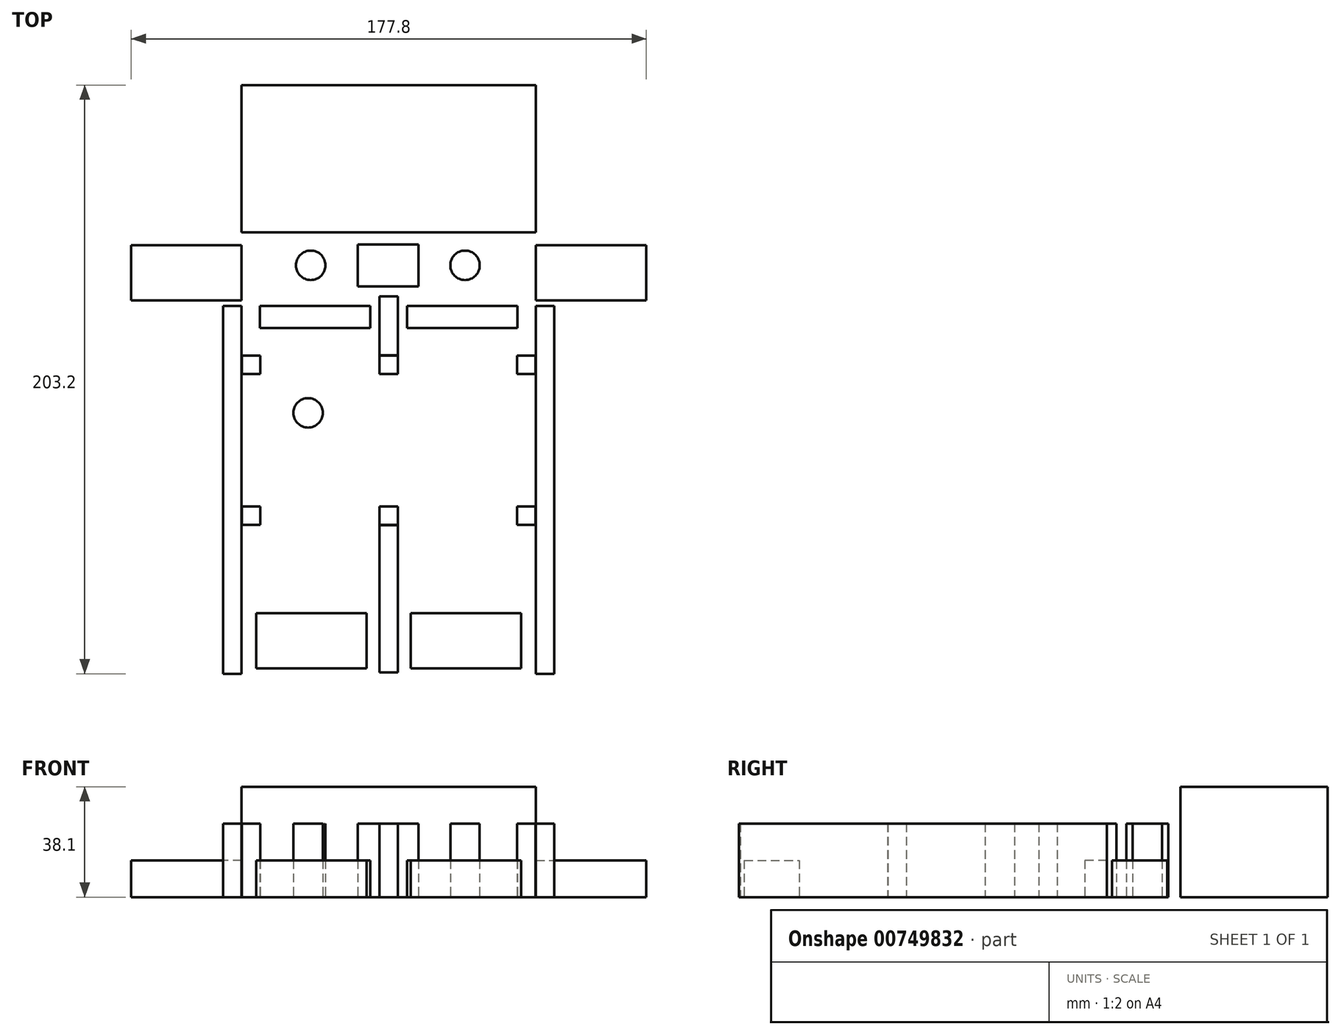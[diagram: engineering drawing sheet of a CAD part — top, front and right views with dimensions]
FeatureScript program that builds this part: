
annotation { "Feature Type Name" : "Feature", "Feature Type Description" : "" }
export const myFeature = defineFeature(function(context is Context, id is Id, definition is map)
    precondition{}
    {
        {
            var Q0;
            Q0=qCreatedBy(makeId("Top.planeOp"),FACE);
            var sketch = newSketch(context, id + "F0", { "sketchPlane" : qUnion([Q0])});
            skLineSegment(sketch, "E0.bottom", {"start": v(50.8, 25.4) * mm, "end": v(-50.8, 25.4) * mm});
            skLineSegment(sketch, "E0.top", {"start": v(50.8, -25.4) * mm, "end": v(-50.8, -25.4) * mm});
            skLineSegment(sketch, "E0.left", {"start": v(50.8, 25.4) * mm, "end": v(50.8, -25.4) * mm});
            skLineSegment(sketch, "E0.right", {"start": v(-50.8, 25.4) * mm, "end": v(-50.8, -25.4) * mm});
            skPoint(sketch, "E0.middle", {"position": v(0, 0) * mm});
            skSolve(sketch);
        }
        {
            var Q0;
            Q0=makeQuery(id+"F0.imprint","IMPRINT",FACE,{"disambiguationData":[TD([[makeQuery(id+"F0.imprint","IMPRINT",EDGE,{"derivedFrom":sQuery(id+"F0.wireOp",EDGE,"E0.bottom")}),1.0]])]});
            extrude(context, id + "F1", {"entities" : qUnion([Q0]), "depth" : 38.1 * mm, "offsetDistance" : 25.4 * mm});
        }
        {
            var Q0;
            Q0=qCreatedBy(makeId("Top.planeOp"),FACE);
            var sketch = newSketch(context, id + "F2", { "sketchPlane" : qUnion([Q0])});
            skLineSegment(sketch, "E1", {"start": v(0, 0) * mm, "end": v(0, -50.8) * mm, "construction": true});
            skLineSegment(sketch, "E2", {"start": v(0, -50.8) * mm, "end": v(-6.35, -50.8) * mm, "construction": true});
            skLineSegment(sketch, "E3", {"start": v(0, -50.8) * mm, "end": v(6.35, -50.8) * mm, "construction": true});
            skLineSegment(sketch, "E4.bottom", {"start": v(-6.35, -50.8) * mm, "end": v(-44.45, -50.8) * mm});
            skLineSegment(sketch, "E4.top", {"start": v(-6.35, -58.43) * mm, "end": v(-44.45, -58.43) * mm});
            skLineSegment(sketch, "E4.left", {"start": v(-6.35, -50.8) * mm, "end": v(-6.35, -58.43) * mm});
            skLineSegment(sketch, "E4.right", {"start": v(-44.45, -50.8) * mm, "end": v(-44.45, -58.43) * mm});
            skLineSegment(sketch, "E5.bottom", {"start": v(6.35, -50.8) * mm, "end": v(44.45, -50.8) * mm});
            skLineSegment(sketch, "E5.top", {"start": v(6.35, -58.43) * mm, "end": v(44.45, -58.43) * mm});
            skLineSegment(sketch, "E5.left", {"start": v(6.35, -50.8) * mm, "end": v(6.35, -58.43) * mm});
            skLineSegment(sketch, "E5.right", {"start": v(44.45, -50.8) * mm, "end": v(44.45, -58.43) * mm});
            skSolve(sketch);
        }
        {
            var Q0;
            Q0 = qSketchRegion(id + "F2", true);
            extrude(context, id + "F3", {"entities" : qUnion([Q0]), "depth" : 12.7 * mm, "offsetDistance" : 25.4 * mm});
        }
        {
            var Q0;
            Q0=qCreatedBy(makeId("Top.planeOp"),FACE);
            var sketch = newSketch(context, id + "F4", { "sketchPlane" : qUnion([Q0])});
            skLineSegment(sketch, "E6.top", {"start": v(-3.18, -67.9) * mm, "end": v(3.17, -67.9) * mm});
            skLineSegment(sketch, "E6.left", {"start": v(-3.18, -47.59) * mm, "end": v(-3.18, -67.9) * mm});
            skLineSegment(sketch, "E6.right", {"start": v(3.17, -47.59) * mm, "end": v(3.17, -67.9) * mm});
            skPoint(sketch, "E6.middle", {"position": v(0, -47.59) * mm});
            skLineSegment(sketch, "E7", {"start": v(3.17, -47.59) * mm, "end": v(-3.18, -47.59) * mm});
            skSolve(sketch);
        }
        {
            var Q0;
            Q0 = qSketchRegion(id + "F4", true);
            extrude(context, id + "F5", {"entities" : qUnion([Q0]), "depth" : 25.4 * mm, "offsetDistance" : 25.4 * mm});
        }
        {
            var Q0;
            Q0=qCreatedBy(makeId("Top.planeOp"),FACE);
            var sketch = newSketch(context, id + "F6", { "sketchPlane" : qUnion([Q0])});
            skLineSegment(sketch, "E8", {"start": v(0, 0) * mm, "end": v(0, -50.8) * mm, "construction": true});
            skLineSegment(sketch, "E9", {"start": v(0, -50.8) * mm, "end": v(50.8, -50.8) * mm, "construction": true});
            skLineSegment(sketch, "E10", {"start": v(0, -50.8) * mm, "end": v(-50.8, -50.8) * mm, "construction": true});
            skLineSegment(sketch, "E11.bottom", {"start": v(-50.8, -50.8) * mm, "end": v(-57.15, -50.8) * mm});
            skLineSegment(sketch, "E11.top", {"start": v(-50.8, -177.8) * mm, "end": v(-57.15, -177.8) * mm});
            skLineSegment(sketch, "E11.left", {"start": v(-50.8, -50.8) * mm, "end": v(-50.8, -177.8) * mm});
            skLineSegment(sketch, "E11.right", {"start": v(-57.15, -50.8) * mm, "end": v(-57.15, -177.8) * mm});
            skLineSegment(sketch, "E12.bottom", {"start": v(50.8, -50.8) * mm, "end": v(57.15, -50.8) * mm});
            skLineSegment(sketch, "E12.top", {"start": v(50.8, -177.8) * mm, "end": v(57.15, -177.8) * mm});
            skLineSegment(sketch, "E12.left", {"start": v(50.8, -50.8) * mm, "end": v(50.8, -177.8) * mm});
            skLineSegment(sketch, "E12.right", {"start": v(57.15, -50.8) * mm, "end": v(57.15, -177.8) * mm});
            skSolve(sketch);
        }
        {
            var Q0;
            Q0=makeQuery(id+"F6.imprint","IMPRINT",FACE,{"disambiguationData":[TD([[makeQuery(id+"F6.imprint","IMPRINT",EDGE,{"derivedFrom":sQuery(id+"F6.wireOp",EDGE,"E11.bottom")}),1.0]])]});
            var Q1;
            Q1=makeQuery(id+"F6.imprint","IMPRINT",FACE,{"disambiguationData":[TD([[makeQuery(id+"F6.imprint","IMPRINT",EDGE,{"derivedFrom":sQuery(id+"F6.wireOp",EDGE,"E12.bottom")}),-1.0]])]});
            extrude(context, id + "F7", {"entities" : qUnion([Q0, Q1]), "depth" : 25.4 * mm, "offsetDistance" : 25.4 * mm});
        }
        {
            var Q0;
            Q0=qCreatedBy(makeId("Top.planeOp"),FACE);
            var sketch = newSketch(context, id + "F8", { "sketchPlane" : qUnion([Q0])});
            skLineSegment(sketch, "E13", {"start": v(0, 0) * mm, "end": v(0, -67.94) * mm});
            skLineSegment(sketch, "E14.bottom", {"start": v(0, -67.94) * mm, "end": v(3.18, -67.94) * mm});
            skLineSegment(sketch, "E14.top", {"start": v(0, -74.3) * mm, "end": v(3.18, -74.3) * mm});
            skLineSegment(sketch, "E14.left", {"start": v(0, -67.94) * mm, "end": v(0, -74.3) * mm});
            skLineSegment(sketch, "E14.right", {"start": v(3.18, -67.95) * mm, "end": v(3.18, -74.3) * mm});
            skLineSegment(sketch, "E15.bottom", {"start": v(0, -74.3) * mm, "end": v(-3.17, -74.3) * mm});
            skLineSegment(sketch, "E15.top", {"start": v(0, -67.94) * mm, "end": v(-3.17, -67.94) * mm});
            skLineSegment(sketch, "E15.left", {"start": v(0, -74.3) * mm, "end": v(0, -67.94) * mm});
            skLineSegment(sketch, "E15.right", {"start": v(-3.17, -74.3) * mm, "end": v(-3.17, -67.95) * mm});
            skLineSegment(sketch, "E16.bottom", {"start": v(50.67, -67.94) * mm, "end": v(44.32, -67.94) * mm});
            skLineSegment(sketch, "E16.top", {"start": v(50.67, -74.3) * mm, "end": v(44.32, -74.3) * mm});
            skLineSegment(sketch, "E16.left", {"start": v(50.67, -67.94) * mm, "end": v(50.67, -74.3) * mm});
            skLineSegment(sketch, "E16.right", {"start": v(44.32, -67.94) * mm, "end": v(44.32, -74.3) * mm});
            skLineSegment(sketch, "E17", {"start": v(3.18, -74.3) * mm, "end": v(44.32, -74.3) * mm, "construction": true});
            skLineSegment(sketch, "E18.bottom", {"start": v(-50.67, -74.3) * mm, "end": v(-44.32, -74.3) * mm});
            skLineSegment(sketch, "E18.top", {"start": v(-50.67, -67.94) * mm, "end": v(-44.32, -67.94) * mm});
            skLineSegment(sketch, "E18.left", {"start": v(-50.67, -74.3) * mm, "end": v(-50.67, -67.94) * mm});
            skLineSegment(sketch, "E18.right", {"start": v(-44.32, -74.3) * mm, "end": v(-44.32, -67.94) * mm});
            skLineSegment(sketch, "E19", {"start": v(-3.17, -74.3) * mm, "end": v(-44.32, -74.3) * mm, "construction": true});
            skLineSegment(sketch, "E20", {"start": v(50.67, -74.3) * mm, "end": v(50.67, -97.15) * mm, "construction": true});
            skLineSegment(sketch, "E21", {"start": v(50.67, -97.15) * mm, "end": v(-50.93, -97.15) * mm, "construction": true});
            skLineSegment(sketch, "E22.MirrorCS", {"start": v(50.67, -120.01) * mm, "end": v(44.32, -120.01) * mm});
            skLineSegment(sketch, "E23.MirrorCS", {"start": v(50.67, -126.36) * mm, "end": v(44.32, -126.36) * mm});
            skLineSegment(sketch, "E24.MirrorCS", {"start": v(50.67, -126.36) * mm, "end": v(50.67, -120.01) * mm});
            skLineSegment(sketch, "E25.MirrorCS", {"start": v(44.32, -126.36) * mm, "end": v(44.32, -120.01) * mm});
            skLineSegment(sketch, "E26.MirrorCS", {"start": v(3.18, -126.36) * mm, "end": v(3.18, -120.01) * mm});
            skLineSegment(sketch, "E27.MirrorCS", {"start": v(0, -120.01) * mm, "end": v(3.18, -120.01) * mm});
            skLineSegment(sketch, "E28.MirrorCS", {"start": v(0, -120.01) * mm, "end": v(-3.17, -120.01) * mm});
            skLineSegment(sketch, "E29.MirrorCS", {"start": v(-3.17, -120.01) * mm, "end": v(-3.17, -126.36) * mm});
            skLineSegment(sketch, "E30.MirrorCS", {"start": v(0, -126.37) * mm, "end": v(-3.17, -126.37) * mm});
            skLineSegment(sketch, "E31.MirrorCS", {"start": v(0, -126.37) * mm, "end": v(3.18, -126.37) * mm});
            skLineSegment(sketch, "E32.MirrorCS", {"start": v(-44.32, -120.02) * mm, "end": v(-44.32, -126.37) * mm});
            skLineSegment(sketch, "E33.MirrorCS", {"start": v(-50.67, -120.02) * mm, "end": v(-44.32, -120.02) * mm});
            skLineSegment(sketch, "E34.MirrorCS", {"start": v(-50.67, -120.02) * mm, "end": v(-50.67, -126.37) * mm});
            skLineSegment(sketch, "E35.MirrorCS", {"start": v(-50.67, -126.37) * mm, "end": v(-44.32, -126.37) * mm});
            skSolve(sketch);
        }
        {
            var Q0;
            Q0 = qSketchRegion(id + "F8", true);
            extrude(context, id + "F9", {"entities" : qUnion([Q0]), "depth" : 25.4 * mm, "offsetDistance" : 25.4 * mm});
        }
        {
            var Q0;
            Q0=qCreatedBy(makeId("Top.planeOp"),FACE);
            var sketch = newSketch(context, id + "F10", { "sketchPlane" : qUnion([Q0])});
            skLineSegment(sketch, "E36", {"start": v(0, 0) * mm, "end": v(0, -126.5) * mm, "construction": true});
            skLineSegment(sketch, "E37", {"start": v(0, -126.5) * mm, "end": v(0, -151.9) * mm, "construction": true});
            skLineSegment(sketch, "E38.bottom", {"start": v(-3.18, -126.5) * mm, "end": v(3.18, -126.5) * mm});
            skLineSegment(sketch, "E38.top", {"start": v(-3.18, -177.3) * mm, "end": v(3.18, -177.3) * mm});
            skLineSegment(sketch, "E38.left", {"start": v(-3.18, -126.5) * mm, "end": v(-3.18, -177.3) * mm});
            skLineSegment(sketch, "E38.right", {"start": v(3.18, -126.5) * mm, "end": v(3.18, -177.3) * mm});
            skPoint(sketch, "E38.middle", {"position": v(0, -151.9) * mm});
            skSolve(sketch);
        }
        {
            var Q0;
            Q0 = qConstructionFilter(qBodyType(qCreatedBy(id + "F10" ,EDGE), BodyType.WIRE), ConstructionObject.NO);
            extrude(context, id + "F11", {"bodyType" : ToolBodyType.SURFACE, "surfaceEntities" : qUnion([Q0]), "depth" : 25.4 * mm, "offsetDistance" : 25.4 * mm});
        }
        {
            var Q0;
            Q0=makeQuery(id+"F10.imprint","IMPRINT",FACE,{"disambiguationData":[TD([[makeQuery(id+"F10.imprint","IMPRINT",EDGE,{"derivedFrom":sQuery(id+"F10.wireOp",EDGE,"E38.bottom")}),-1.0]])]});
            extrude(context, id + "F12", {"entities" : qUnion([Q0]), "depth" : 25.4 * mm, "offsetDistance" : 25.4 * mm});
        }
        {
            var Q0;
            Q0=qCreatedBy(makeId("Top.planeOp"),FACE);
            var sketch = newSketch(context, id + "F13", { "sketchPlane" : qUnion([Q0])});
            skLineSegment(sketch, "E39.bottom", {"start": v(-50.8, -49) * mm, "end": v(-88.9, -49) * mm});
            skLineSegment(sketch, "E39.top", {"start": v(-50.8, -29.95) * mm, "end": v(-88.9, -29.95) * mm});
            skLineSegment(sketch, "E39.left", {"start": v(-50.8, -49) * mm, "end": v(-50.8, -29.95) * mm});
            skLineSegment(sketch, "E39.right", {"start": v(-88.9, -49) * mm, "end": v(-88.9, -29.95) * mm});
            skLineSegment(sketch, "E40", {"start": v(0, 0) * mm, "end": v(0, -29.95) * mm, "construction": true});
            skLineSegment(sketch, "E41", {"start": v(0, -29.95) * mm, "end": v(-50.8, -29.95) * mm, "construction": true});
            skLineSegment(sketch, "E42.MirrorCS", {"start": v(50.8, -49) * mm, "end": v(50.8, -29.95) * mm});
            skLineSegment(sketch, "E43.MirrorCS", {"start": v(50.8, -29.95) * mm, "end": v(88.9, -29.95) * mm});
            skLineSegment(sketch, "E44.MirrorCS", {"start": v(88.9, -49) * mm, "end": v(88.9, -29.95) * mm});
            skLineSegment(sketch, "E45.MirrorCS", {"start": v(50.8, -49) * mm, "end": v(88.9, -49) * mm});
            skLineSegment(sketch, "E46.bottom", {"start": v(-45.72, -176) * mm, "end": v(-7.62, -176) * mm});
            skLineSegment(sketch, "E46.top", {"start": v(-45.72, -156.95) * mm, "end": v(-7.62, -156.95) * mm});
            skLineSegment(sketch, "E46.left", {"start": v(-45.72, -176) * mm, "end": v(-45.72, -156.95) * mm});
            skLineSegment(sketch, "E46.right", {"start": v(-7.62, -176) * mm, "end": v(-7.62, -156.95) * mm});
            skLineSegment(sketch, "E47", {"start": v(0, -29.95) * mm, "end": v(0, -156.95) * mm, "construction": true});
            skLineSegment(sketch, "E48", {"start": v(0, -156.95) * mm, "end": v(-7.62, -156.95) * mm, "construction": true});
            skLineSegment(sketch, "E49.MirrorCS", {"start": v(45.72, -156.95) * mm, "end": v(7.62, -156.95) * mm});
            skLineSegment(sketch, "E50.MirrorCS", {"start": v(7.62, -176) * mm, "end": v(7.62, -156.95) * mm});
            skLineSegment(sketch, "E51.MirrorCS", {"start": v(45.72, -176) * mm, "end": v(7.62, -176) * mm});
            skLineSegment(sketch, "E52.MirrorCS", {"start": v(45.72, -176) * mm, "end": v(45.72, -156.95) * mm});
            skSolve(sketch);
        }
        {
            var Q0;
            Q0=makeQuery(id+"F13.imprint","IMPRINT",FACE,{"disambiguationData":[TD([[makeQuery(id+"F13.imprint","IMPRINT",EDGE,{"derivedFrom":sQuery(id+"F13.wireOp",EDGE,"E39.bottom")}),-1.0]])]});
            var Q1;
            Q1=makeQuery(id+"F13.imprint","IMPRINT",FACE,{"disambiguationData":[TD([[makeQuery(id+"F13.imprint","IMPRINT",EDGE,{"derivedFrom":sQuery(id+"F13.wireOp",EDGE,"E42.MirrorCS")}),-1.0]])]});
            var Q2;
            Q2=makeQuery(id+"F13.imprint","IMPRINT",FACE,{"disambiguationData":[TD([[makeQuery(id+"F13.imprint","IMPRINT",EDGE,{"derivedFrom":sQuery(id+"F13.wireOp",EDGE,"E49.MirrorCS")}),1.0]])]});
            var Q3;
            Q3=makeQuery(id+"F13.imprint","IMPRINT",FACE,{"disambiguationData":[TD([[makeQuery(id+"F13.imprint","IMPRINT",EDGE,{"derivedFrom":sQuery(id+"F13.wireOp",EDGE,"E46.bottom")}),1.0]])]});
            extrude(context, id + "F14", {"entities" : qUnion([Q0, Q1, Q2, Q3]), "depth" : 12.7 * mm, "offsetDistance" : 25.4 * mm});
        }
        {
            var Q0;
            Q0=qCreatedBy(makeId("Top.planeOp"),FACE);
            var sketch = newSketch(context, id + "F15", { "sketchPlane" : qUnion([Q0])});
            skCircle(sketch, "E53", {"center": v(-27.85, -87.76) * mm, "radius": 5.08 * mm});
            skCircle(sketch, "E54", {"center": v(-26.93, -36.84) * mm, "radius": 5.08 * mm});
            skCircle(sketch, "E55", {"center": v(26.32, -36.84) * mm, "radius": 5.08 * mm});
            skSolve(sketch);
        }
        {
            var Q0;
            Q0 = qSketchRegion(id + "F15", true);
            extrude(context, id + "F16", {"entities" : qUnion([Q0]), "depth" : 25.4 * mm, "offsetDistance" : 25.4 * mm});
        }
        {
            var Q0;
            Q0=qCreatedBy(makeId("Top.planeOp"),FACE);
            var sketch = newSketch(context, id + "F17", { "sketchPlane" : qUnion([Q0])});
            skLineSegment(sketch, "E56.bottom", {"start": v(-10.7, -29.68) * mm, "end": v(10.29, -29.68) * mm});
            skLineSegment(sketch, "E56.top", {"start": v(-10.7, -44.14) * mm, "end": v(10.29, -44.14) * mm});
            skLineSegment(sketch, "E56.left", {"start": v(-10.7, -29.68) * mm, "end": v(-10.7, -44.14) * mm});
            skLineSegment(sketch, "E56.right", {"start": v(10.29, -29.68) * mm, "end": v(10.29, -44.14) * mm});
            skSolve(sketch);
        }
        {
            var Q0;
            Q0 = qSketchRegion(id + "F17", true);
            extrude(context, id + "F18", {"entities" : qUnion([Q0]), "depth" : 25.4 * mm, "offsetDistance" : 25.4 * mm});
        }
    });
